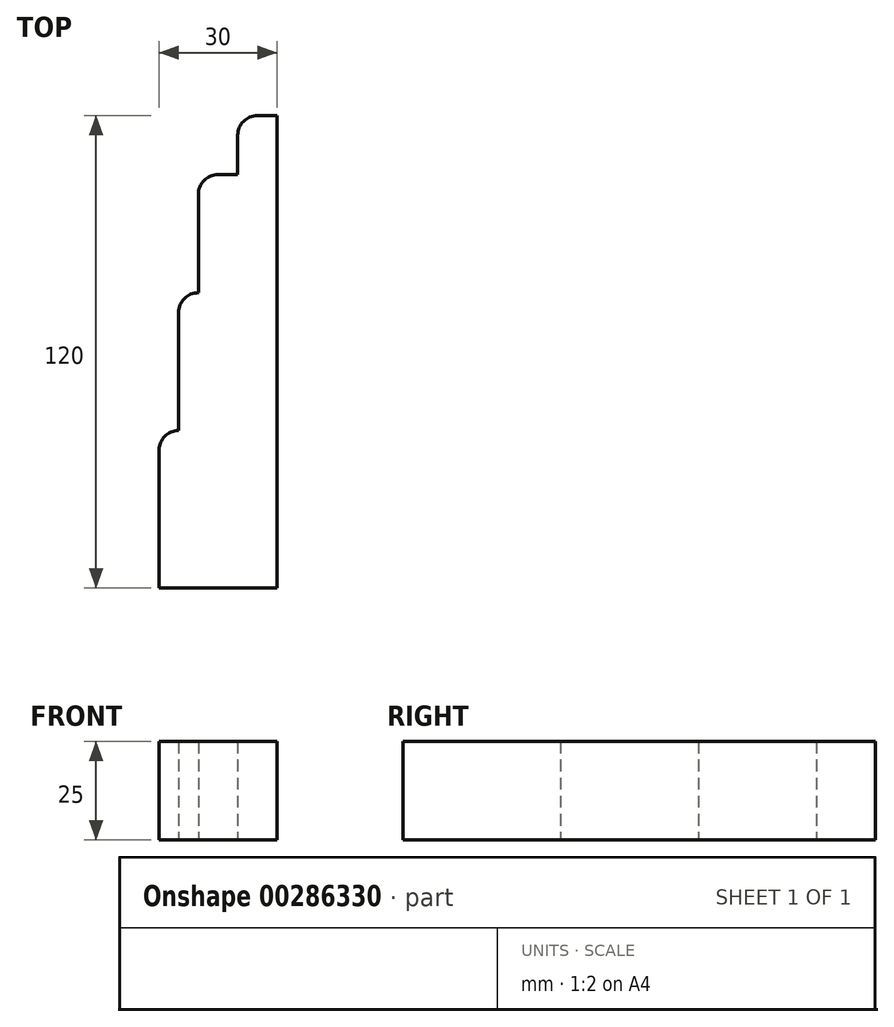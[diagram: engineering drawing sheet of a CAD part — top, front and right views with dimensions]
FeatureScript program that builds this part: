
annotation { "Feature Type Name" : "Feature", "Feature Type Description" : "" }
export const myFeature = defineFeature(function(context is Context, id is Id, definition is map)
    precondition{}
    {
        {
            var Q0;
            Q0=qCreatedBy(makeId("Top.planeOp"),FACE);
            var sketch = newSketch(context, id + "F0", { "sketchPlane" : qUnion([Q0])});
            skLineSegment(sketch, "E0", {"start": v(34.4, -43.13) * mm, "end": v(24.4, -43.13) * mm});
            skLineSegment(sketch, "E1", {"start": v(24.4, -43.13) * mm, "end": v(14.4, -43.13) * mm});
            skLineSegment(sketch, "E2", {"start": v(14.4, -43.13) * mm, "end": v(9.4, -43.13) * mm});
            skLineSegment(sketch, "E3", {"start": v(9.4, -43.13) * mm, "end": v(4.4, -43.13) * mm});
            skLineSegment(sketch, "E4", {"start": v(4.4, -43.13) * mm, "end": v(4.4, -8.13) * mm});
            skLineSegment(sketch, "E5", {"start": v(9.4, -3.13) * mm, "end": v(9.4, -3.13) * mm});
            skLineSegment(sketch, "E6", {"start": v(9.4, -3.13) * mm, "end": v(9.4, 26.87) * mm});
            skLineSegment(sketch, "E7", {"start": v(14.4, 31.87) * mm, "end": v(14.4, 31.87) * mm});
            skLineSegment(sketch, "E8", {"start": v(14.4, 31.87) * mm, "end": v(14.4, 56.87) * mm});
            skLineSegment(sketch, "E9", {"start": v(19.4, 61.87) * mm, "end": v(24.4, 61.87) * mm});
            skLineSegment(sketch, "E10", {"start": v(24.4, 61.87) * mm, "end": v(24.4, 71.87) * mm});
            skLineSegment(sketch, "E11", {"start": v(29.4, 76.87) * mm, "end": v(34.4, 76.87) * mm});
            skLineSegment(sketch, "E12", {"start": v(34.4, 76.87) * mm, "end": v(34.4, -43.13) * mm});
            skPoint(sketch, "E13.visualSharp", {"position": v(24.4, 76.87) * mm});
            skArc(sketch, "E13.filletArc", {"start": v(29.4, 76.87) * mm, "mid": v(25.87, 75.41) * mm, "end": v(24.4, 71.87) * mm});
            skPoint(sketch, "E14.visualSharp", {"position": v(14.4, 61.87) * mm});
            skArc(sketch, "E14.filletArc", {"start": v(19.4, 61.87) * mm, "mid": v(15.87, 60.41) * mm, "end": v(14.4, 56.87) * mm});
            skPoint(sketch, "E15.visualSharp", {"position": v(9.4, 31.87) * mm});
            skArc(sketch, "E15.filletArc", {"start": v(14.4, 31.87) * mm, "mid": v(10.87, 30.41) * mm, "end": v(9.4, 26.87) * mm});
            skPoint(sketch, "E16.visualSharp", {"position": v(4.4, -3.13) * mm});
            skArc(sketch, "E16.filletArc", {"start": v(9.4, -3.13) * mm, "mid": v(5.87, -4.59) * mm, "end": v(4.4, -8.13) * mm});
            skSolve(sketch);
        }
        {
            var Q0;
            Q0 = qSketchRegion(id + "F0", true);
            extrude(context, id + "F1", {"entities" : qUnion([Q0]), "depth" : 25 * mm});
        }
    });
